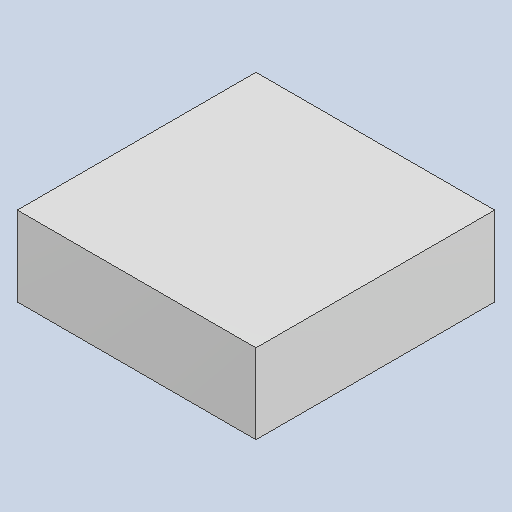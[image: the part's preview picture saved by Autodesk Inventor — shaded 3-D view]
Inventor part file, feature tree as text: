
AUTODESK INVENTOR PART (.ipt)
format: ipt  version: 2023.4 (Build 274418000, 418)  size: 79,872 bytes
history: native  units: mm
features: extrude x1
ambient origin geometry x8: Origin, YZ Plane, XZ Plane, XY Plane, X Axis, Y Axis, Z Axis, Center Point
bodies: Solid1 (feature_tree)
feature tree (1):
  extrude  "Extruded_18"  [1 undecoded]
note: 1 required parameter value undecoded (feature->parameter linkage not recoverable at this tier; creation-order binding heuristic only, values carry confidence <= 0.55)
